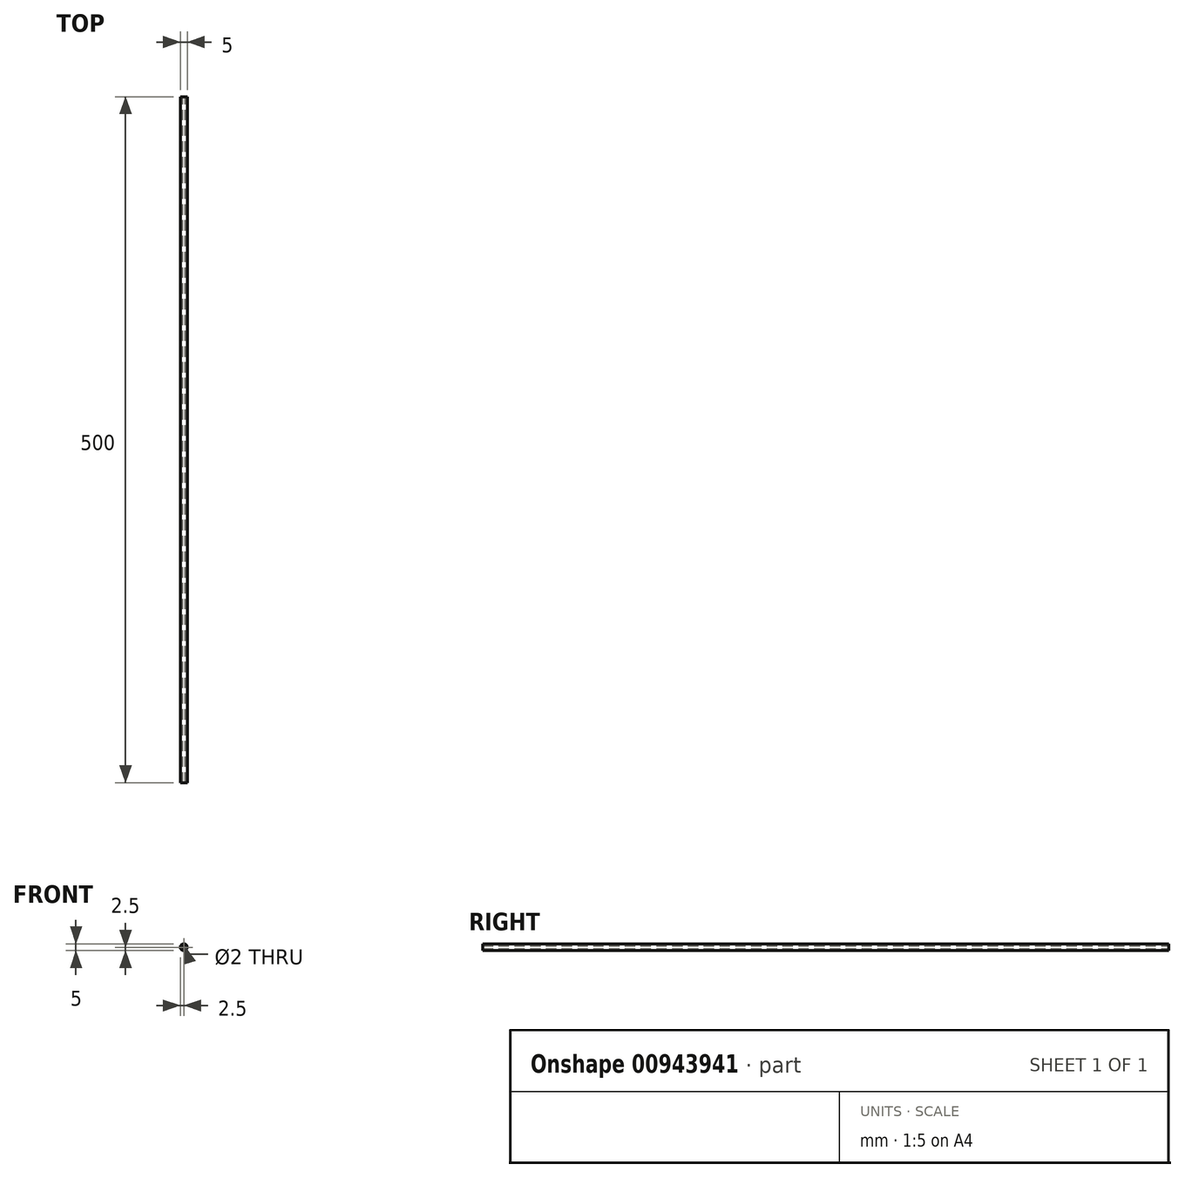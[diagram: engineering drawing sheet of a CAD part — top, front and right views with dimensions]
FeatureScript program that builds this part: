
annotation { "Feature Type Name" : "Feature", "Feature Type Description" : "" }
export const myFeature = defineFeature(function(context is Context, id is Id, definition is map)
    precondition{}
    {
        {
            var Q0;
            Q0=qCreatedBy(makeId("Front.planeOp"),FACE);
            var sketch = newSketch(context, id + "F0", { "sketchPlane" : qUnion([Q0])});
            skCircle(sketch, "E0", {"center": v(0, 0) * mm, "radius": 2.5 * mm});
            skCircle(sketch, "E1", {"center": v(0, 0) * mm, "radius": 1 * mm});
            skSolve(sketch);
        }
        {
            var Q0;
            Q0 = qSketchRegion(id + "F0", true);
            extrude(context, id + "F1", {"entities" : qUnion([Q0]), "depth" : 500 * mm, "offsetDistance" : 25 * mm});
        }
    });
